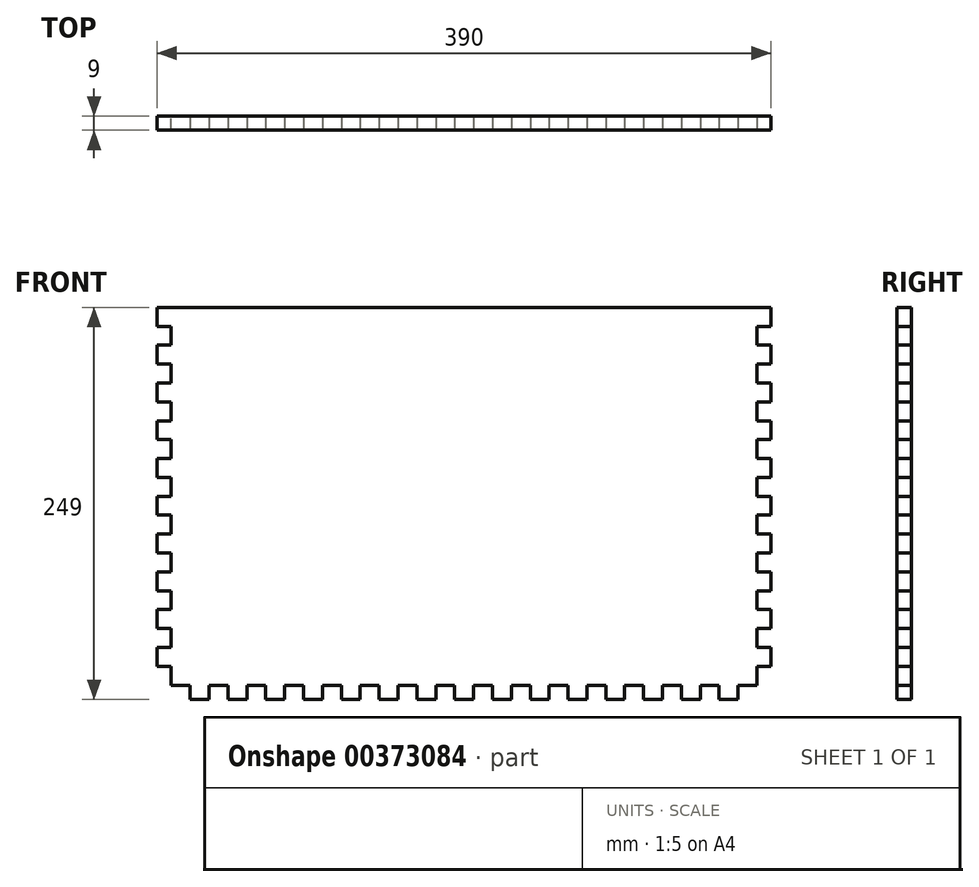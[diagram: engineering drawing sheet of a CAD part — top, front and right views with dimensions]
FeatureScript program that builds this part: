
annotation { "Feature Type Name" : "Feature", "Feature Type Description" : "" }
export const myFeature = defineFeature(function(context is Context, id is Id, definition is map)
    precondition{}
    {
        {
            var Q0;
            Q0=qCreatedBy(makeId("Front.planeOp"),FACE);
            var sketch = newSketch(context, id + "F0", { "sketchPlane" : qUnion([Q0])});
            skLineSegment(sketch, "E0.bottom", {"start": v(186, 120) * mm, "end": v(-186, 120) * mm});
            skLineSegment(sketch, "E0.top", {"start": v(186, -120) * mm, "end": v(-186, -120) * mm});
            skLineSegment(sketch, "E0.left", {"start": v(186, 120) * mm, "end": v(186, -120) * mm});
            skLineSegment(sketch, "E0.right", {"start": v(-186, 120) * mm, "end": v(-186, -120) * mm});
            skPoint(sketch, "E0.middle", {"position": v(0, 0) * mm});
            skSolve(sketch);
        }
        {
            var Q0;
            Q0=makeQuery(id+"F0.imprint","IMPRINT",FACE,{"disambiguationData":[TD([[makeQuery(id+"F0.imprint","IMPRINT",EDGE,{"derivedFrom":sQuery(id+"F0.wireOp",EDGE,"E0.bottom")}),1.0]])]});
            extrude(context, id + "F1", {"entities" : qUnion([Q0]), "depth" : 9 * mm});
        }
        {
            var Q0;
            Q0=makeQuery(id+"F1.opExtrude","CAP_FACE",FACE,{"disambiguationData":[OSD([sQuery(id+"F0.wireOp",EDGE,"E0.bottom"),sQuery(id+"F0.wireOp",EDGE,"E0.top"),sQuery(id+"F0.wireOp",EDGE,"E0.left"),sQuery(id+"F0.wireOp",EDGE,"E0.right")])],"isStart":false});
            var sketch = newSketch(context, id + "F2", { "sketchPlane" : qUnion([Q0])});
            skLineSegment(sketch, "E1.bottom", {"start": v(-186, 120) * mm, "end": v(-195, 120) * mm});
            skLineSegment(sketch, "E1.top", {"start": v(-186, 108) * mm, "end": v(-195, 108) * mm});
            skLineSegment(sketch, "E1.left", {"start": v(-186, 120) * mm, "end": v(-186, 108) * mm});
            skLineSegment(sketch, "E1.right", {"start": v(-195, 120) * mm, "end": v(-195, 108) * mm});
            skLineSegment(sketch, "E2.0.1.0", {"start": v(-186, 84) * mm, "end": v(-195, 84) * mm});
            skLineSegment(sketch, "E2.0.1.1", {"start": v(-195, 96) * mm, "end": v(-195, 84) * mm});
            skLineSegment(sketch, "E2.0.1.2", {"start": v(-186, 96) * mm, "end": v(-195, 96) * mm});
            skLineSegment(sketch, "E2.0.1.3", {"start": v(-186, 96) * mm, "end": v(-186, 84) * mm});
            skLineSegment(sketch, "E2.0.2.0", {"start": v(-186, 60) * mm, "end": v(-195, 60) * mm});
            skLineSegment(sketch, "E2.0.2.1", {"start": v(-195, 72) * mm, "end": v(-195, 60) * mm});
            skLineSegment(sketch, "E2.0.2.2", {"start": v(-186, 72) * mm, "end": v(-195, 72) * mm});
            skLineSegment(sketch, "E2.0.2.3", {"start": v(-186, 72) * mm, "end": v(-186, 60) * mm});
            skLineSegment(sketch, "E2.0.3.0", {"start": v(-186, 36) * mm, "end": v(-195, 36) * mm});
            skLineSegment(sketch, "E2.0.3.1", {"start": v(-195, 48) * mm, "end": v(-195, 36) * mm});
            skLineSegment(sketch, "E2.0.3.2", {"start": v(-186, 48) * mm, "end": v(-195, 48) * mm});
            skLineSegment(sketch, "E2.0.3.3", {"start": v(-186, 48) * mm, "end": v(-186, 36) * mm});
            skLineSegment(sketch, "E2.0.4.0", {"start": v(-186, 12) * mm, "end": v(-195, 12) * mm});
            skLineSegment(sketch, "E2.0.4.1", {"start": v(-195, 24) * mm, "end": v(-195, 12) * mm});
            skLineSegment(sketch, "E2.0.4.2", {"start": v(-186, 24) * mm, "end": v(-195, 24) * mm});
            skLineSegment(sketch, "E2.0.4.3", {"start": v(-186, 24) * mm, "end": v(-186, 12) * mm});
            skLineSegment(sketch, "E2.0.5.0", {"start": v(-186, -12) * mm, "end": v(-195, -12) * mm});
            skLineSegment(sketch, "E2.0.5.1", {"start": v(-195, 0) * mm, "end": v(-195, -12) * mm});
            skLineSegment(sketch, "E2.0.5.2", {"start": v(-186, 0) * mm, "end": v(-195, 0) * mm});
            skLineSegment(sketch, "E2.0.5.3", {"start": v(-186, 0) * mm, "end": v(-186, -12) * mm});
            skLineSegment(sketch, "E2.0.6.0", {"start": v(-186, -36) * mm, "end": v(-195, -36) * mm});
            skLineSegment(sketch, "E2.0.6.1", {"start": v(-195, -24) * mm, "end": v(-195, -36) * mm});
            skLineSegment(sketch, "E2.0.6.2", {"start": v(-186, -24) * mm, "end": v(-195, -24) * mm});
            skLineSegment(sketch, "E2.0.6.3", {"start": v(-186, -24) * mm, "end": v(-186, -36) * mm});
            skLineSegment(sketch, "E2.0.7.0", {"start": v(-186, -60) * mm, "end": v(-195, -60) * mm});
            skLineSegment(sketch, "E2.0.7.1", {"start": v(-195, -48) * mm, "end": v(-195, -60) * mm});
            skLineSegment(sketch, "E2.0.7.2", {"start": v(-186, -48) * mm, "end": v(-195, -48) * mm});
            skLineSegment(sketch, "E2.0.7.3", {"start": v(-186, -48) * mm, "end": v(-186, -60) * mm});
            skLineSegment(sketch, "E2.0.8.0", {"start": v(-186, -84) * mm, "end": v(-195, -84) * mm});
            skLineSegment(sketch, "E2.0.8.1", {"start": v(-195, -72) * mm, "end": v(-195, -84) * mm});
            skLineSegment(sketch, "E2.0.8.2", {"start": v(-186, -72) * mm, "end": v(-195, -72) * mm});
            skLineSegment(sketch, "E2.0.8.3", {"start": v(-186, -72) * mm, "end": v(-186, -84) * mm});
            skLineSegment(sketch, "E2.0.9.0", {"start": v(-186, -108) * mm, "end": v(-195, -108) * mm});
            skLineSegment(sketch, "E2.0.9.1", {"start": v(-195, -96) * mm, "end": v(-195, -108) * mm});
            skLineSegment(sketch, "E2.0.9.2", {"start": v(-186, -96) * mm, "end": v(-195, -96) * mm});
            skLineSegment(sketch, "E2.0.9.3", {"start": v(-186, -96) * mm, "end": v(-186, -108) * mm});
            skLineSegment(sketch, "E2.direction1", {"start": v(-195, 108) * mm, "end": v(-186, 108) * mm, "construction": true});
            skLineSegment(sketch, "E2.direction2", {"start": v(-195, 108) * mm, "end": v(-195, 84) * mm, "construction": true});
            skLineSegment(sketch, "E3", {"start": v(0, 120) * mm, "end": v(0, 0) * mm});
            skLineSegment(sketch, "E4.MirrorCS", {"start": v(186, 108) * mm, "end": v(195, 108) * mm});
            skLineSegment(sketch, "E5.MirrorCS", {"start": v(195, 108) * mm, "end": v(186, 108) * mm, "construction": true});
            skLineSegment(sketch, "E6.MirrorCS", {"start": v(195, 96) * mm, "end": v(195, 84) * mm});
            skLineSegment(sketch, "E7.MirrorCS", {"start": v(186, -24) * mm, "end": v(186, -36) * mm});
            skLineSegment(sketch, "E8.MirrorCS", {"start": v(186, -96) * mm, "end": v(186, -108) * mm});
            skLineSegment(sketch, "E9.MirrorCS", {"start": v(186, 0) * mm, "end": v(186, -12) * mm});
            skLineSegment(sketch, "E10.MirrorCS", {"start": v(186, -108) * mm, "end": v(195, -108) * mm});
            skLineSegment(sketch, "E11.MirrorCS", {"start": v(195, -48) * mm, "end": v(195, -60) * mm});
            skLineSegment(sketch, "E12.MirrorCS", {"start": v(186, -12) * mm, "end": v(195, -12) * mm});
            skLineSegment(sketch, "E13.MirrorCS", {"start": v(186, -84) * mm, "end": v(195, -84) * mm});
            skLineSegment(sketch, "E14.MirrorCS", {"start": v(186, 12) * mm, "end": v(195, 12) * mm});
            skLineSegment(sketch, "E15.MirrorCS", {"start": v(186, -60) * mm, "end": v(195, -60) * mm});
            skLineSegment(sketch, "E16.MirrorCS", {"start": v(186, -36) * mm, "end": v(195, -36) * mm});
            skLineSegment(sketch, "E17.MirrorCS", {"start": v(195, -96) * mm, "end": v(195, -108) * mm});
            skLineSegment(sketch, "E18.MirrorCS", {"start": v(186, -48) * mm, "end": v(195, -48) * mm});
            skLineSegment(sketch, "E19.MirrorCS", {"start": v(195, 0) * mm, "end": v(195, -12) * mm});
            skLineSegment(sketch, "E20.MirrorCS", {"start": v(195, -72) * mm, "end": v(195, -84) * mm});
            skLineSegment(sketch, "E21.MirrorCS", {"start": v(195, 24) * mm, "end": v(195, 12) * mm});
            skLineSegment(sketch, "E22.MirrorCS", {"start": v(195, 48) * mm, "end": v(195, 36) * mm});
            skLineSegment(sketch, "E23.MirrorCS", {"start": v(186, 48) * mm, "end": v(195, 48) * mm});
            skLineSegment(sketch, "E24.MirrorCS", {"start": v(186, 48) * mm, "end": v(186, 36) * mm});
            skLineSegment(sketch, "E25.MirrorCS", {"start": v(186, 120) * mm, "end": v(195, 120) * mm});
            skLineSegment(sketch, "E26.MirrorCS", {"start": v(186, 120) * mm, "end": v(186, 108) * mm});
            skLineSegment(sketch, "E27.MirrorCS", {"start": v(195, 120) * mm, "end": v(195, 108) * mm});
            skLineSegment(sketch, "E28.MirrorCS", {"start": v(186, 84) * mm, "end": v(195, 84) * mm});
            skLineSegment(sketch, "E29.MirrorCS", {"start": v(186, 96) * mm, "end": v(195, 96) * mm});
            skLineSegment(sketch, "E30.MirrorCS", {"start": v(186, 96) * mm, "end": v(186, 84) * mm});
            skLineSegment(sketch, "E31.MirrorCS", {"start": v(186, 60) * mm, "end": v(195, 60) * mm});
            skLineSegment(sketch, "E32.MirrorCS", {"start": v(195, 72) * mm, "end": v(195, 60) * mm});
            skLineSegment(sketch, "E33.MirrorCS", {"start": v(186, 72) * mm, "end": v(195, 72) * mm});
            skLineSegment(sketch, "E34.MirrorCS", {"start": v(186, 72) * mm, "end": v(186, 60) * mm});
            skLineSegment(sketch, "E35.MirrorCS", {"start": v(195, 108) * mm, "end": v(195, 84) * mm, "construction": true});
            skLineSegment(sketch, "E36.MirrorCS", {"start": v(195, -24) * mm, "end": v(195, -36) * mm});
            skLineSegment(sketch, "E37.MirrorCS", {"start": v(186, 36) * mm, "end": v(195, 36) * mm});
            skLineSegment(sketch, "E38.MirrorCS", {"start": v(186, -96) * mm, "end": v(195, -96) * mm});
            skLineSegment(sketch, "E39.MirrorCS", {"start": v(186, -48) * mm, "end": v(186, -60) * mm});
            skLineSegment(sketch, "E40.MirrorCS", {"start": v(186, 0) * mm, "end": v(195, 0) * mm});
            skLineSegment(sketch, "E41.MirrorCS", {"start": v(186, -72) * mm, "end": v(195, -72) * mm});
            skLineSegment(sketch, "E42.MirrorCS", {"start": v(186, 24) * mm, "end": v(195, 24) * mm});
            skLineSegment(sketch, "E43.MirrorCS", {"start": v(186, -24) * mm, "end": v(195, -24) * mm});
            skLineSegment(sketch, "E44.MirrorCS", {"start": v(186, -72) * mm, "end": v(186, -84) * mm});
            skLineSegment(sketch, "E45.MirrorCS", {"start": v(186, 24) * mm, "end": v(186, 12) * mm});
            skSolve(sketch);
        }
        {
            var Q0;
            Q0 = qSketchRegion(id + "F2", true);
            var Q1;
            Q1=makeQuery(id+"F1.opExtrude","CAP_FACE",FACE,{"disambiguationData":[OSD([sQuery(id+"F0.wireOp",EDGE,"E0.bottom"),sQuery(id+"F0.wireOp",EDGE,"E0.top"),sQuery(id+"F0.wireOp",EDGE,"E0.left"),sQuery(id+"F0.wireOp",EDGE,"E0.right")])],"isStart":true});
            extrude(context, id + "F3", {"entities" : qUnion([Q0]), "operationType" : NewBodyOperationType.ADD, "endBound" : BoundingType.UP_TO_SURFACE, "oppositeDirection" : true, "endBoundEntityFace" : qUnion([Q1]), "depth" : 25 * mm});
        }
        {
            var Q0;
            Q0=makeQuery(id+"F3.boolean.opBoolean","MERGE",FACE,{"derivedFrom":[makeQuery(id+"F1.opExtrude","CAP_FACE",FACE,{"disambiguationData":[OSD([sQuery(id+"F0.wireOp",EDGE,"E0.bottom"),sQuery(id+"F0.wireOp",EDGE,"E0.top"),sQuery(id+"F0.wireOp",EDGE,"E0.left"),sQuery(id+"F0.wireOp",EDGE,"E0.right")])],"isStart":false}),makeQuery(id+"F3.opExtrude","CAP_FACE",FACE,{"disambiguationData":[OSD([sQuery(id+"F2.wireOp",EDGE,"E1.bottom"),sQuery(id+"F2.wireOp",EDGE,"E1.top"),sQuery(id+"F2.wireOp",EDGE,"E1.left"),sQuery(id+"F2.wireOp",EDGE,"E1.right")])],"isStart":true}),makeQuery(id+"F3.opExtrude","CAP_FACE",FACE,{"disambiguationData":[OSD([sQuery(id+"F2.wireOp",EDGE,"E2.0.1.0"),sQuery(id+"F2.wireOp",EDGE,"E2.0.1.1"),sQuery(id+"F2.wireOp",EDGE,"E2.0.1.2"),sQuery(id+"F2.wireOp",EDGE,"E2.0.1.3")])],"isStart":true}),makeQuery(id+"F3.opExtrude","CAP_FACE",FACE,{"disambiguationData":[OSD([sQuery(id+"F2.wireOp",EDGE,"E2.0.2.0"),sQuery(id+"F2.wireOp",EDGE,"E2.0.2.1"),sQuery(id+"F2.wireOp",EDGE,"E2.0.2.2"),sQuery(id+"F2.wireOp",EDGE,"E2.0.2.3")])],"isStart":true}),makeQuery(id+"F3.opExtrude","CAP_FACE",FACE,{"disambiguationData":[OSD([sQuery(id+"F2.wireOp",EDGE,"E2.0.3.0"),sQuery(id+"F2.wireOp",EDGE,"E2.0.3.1"),sQuery(id+"F2.wireOp",EDGE,"E2.0.3.2"),sQuery(id+"F2.wireOp",EDGE,"E2.0.3.3")])],"isStart":true}),makeQuery(id+"F3.opExtrude","CAP_FACE",FACE,{"disambiguationData":[OSD([sQuery(id+"F2.wireOp",EDGE,"E2.0.4.0"),sQuery(id+"F2.wireOp",EDGE,"E2.0.4.1"),sQuery(id+"F2.wireOp",EDGE,"E2.0.4.2"),sQuery(id+"F2.wireOp",EDGE,"E2.0.4.3")])],"isStart":true}),makeQuery(id+"F3.opExtrude","CAP_FACE",FACE,{"disambiguationData":[OSD([sQuery(id+"F2.wireOp",EDGE,"E2.0.5.0"),sQuery(id+"F2.wireOp",EDGE,"E2.0.5.1"),sQuery(id+"F2.wireOp",EDGE,"E2.0.5.2"),sQuery(id+"F2.wireOp",EDGE,"E2.0.5.3")])],"isStart":true}),makeQuery(id+"F3.opExtrude","CAP_FACE",FACE,{"disambiguationData":[OSD([sQuery(id+"F2.wireOp",EDGE,"E2.0.6.0"),sQuery(id+"F2.wireOp",EDGE,"E2.0.6.1"),sQuery(id+"F2.wireOp",EDGE,"E2.0.6.2"),sQuery(id+"F2.wireOp",EDGE,"E2.0.6.3")])],"isStart":true}),makeQuery(id+"F3.opExtrude","CAP_FACE",FACE,{"disambiguationData":[OSD([sQuery(id+"F2.wireOp",EDGE,"E2.0.7.0"),sQuery(id+"F2.wireOp",EDGE,"E2.0.7.1"),sQuery(id+"F2.wireOp",EDGE,"E2.0.7.2"),sQuery(id+"F2.wireOp",EDGE,"E2.0.7.3")])],"isStart":true}),makeQuery(id+"F3.opExtrude","CAP_FACE",FACE,{"disambiguationData":[OSD([sQuery(id+"F2.wireOp",EDGE,"E2.0.8.0"),sQuery(id+"F2.wireOp",EDGE,"E2.0.8.1"),sQuery(id+"F2.wireOp",EDGE,"E2.0.8.2"),sQuery(id+"F2.wireOp",EDGE,"E2.0.8.3")])],"isStart":true}),makeQuery(id+"F3.opExtrude","CAP_FACE",FACE,{"disambiguationData":[OSD([sQuery(id+"F2.wireOp",EDGE,"E2.0.9.0"),sQuery(id+"F2.wireOp",EDGE,"E2.0.9.1"),sQuery(id+"F2.wireOp",EDGE,"E2.0.9.2"),sQuery(id+"F2.wireOp",EDGE,"E2.0.9.3")])],"isStart":true}),makeQuery(id+"F3.opExtrude","CAP_FACE",FACE,{"disambiguationData":[OSD([sQuery(id+"F2.wireOp",EDGE,"E4.MirrorCS"),sQuery(id+"F2.wireOp",EDGE,"E25.MirrorCS"),sQuery(id+"F2.wireOp",EDGE,"E26.MirrorCS"),sQuery(id+"F2.wireOp",EDGE,"E27.MirrorCS")])],"isStart":true}),makeQuery(id+"F3.opExtrude","CAP_FACE",FACE,{"disambiguationData":[OSD([sQuery(id+"F2.wireOp",EDGE,"E6.MirrorCS"),sQuery(id+"F2.wireOp",EDGE,"E28.MirrorCS"),sQuery(id+"F2.wireOp",EDGE,"E29.MirrorCS"),sQuery(id+"F2.wireOp",EDGE,"E30.MirrorCS")])],"isStart":true}),makeQuery(id+"F3.opExtrude","CAP_FACE",FACE,{"disambiguationData":[OSD([sQuery(id+"F2.wireOp",EDGE,"E7.MirrorCS"),sQuery(id+"F2.wireOp",EDGE,"E16.MirrorCS"),sQuery(id+"F2.wireOp",EDGE,"E36.MirrorCS"),sQuery(id+"F2.wireOp",EDGE,"E43.MirrorCS")])],"isStart":true}),makeQuery(id+"F3.opExtrude","CAP_FACE",FACE,{"disambiguationData":[OSD([sQuery(id+"F2.wireOp",EDGE,"E8.MirrorCS"),sQuery(id+"F2.wireOp",EDGE,"E10.MirrorCS"),sQuery(id+"F2.wireOp",EDGE,"E17.MirrorCS"),sQuery(id+"F2.wireOp",EDGE,"E38.MirrorCS")])],"isStart":true}),makeQuery(id+"F3.opExtrude","CAP_FACE",FACE,{"disambiguationData":[OSD([sQuery(id+"F2.wireOp",EDGE,"E9.MirrorCS"),sQuery(id+"F2.wireOp",EDGE,"E12.MirrorCS"),sQuery(id+"F2.wireOp",EDGE,"E19.MirrorCS"),sQuery(id+"F2.wireOp",EDGE,"E40.MirrorCS")])],"isStart":true}),makeQuery(id+"F3.opExtrude","CAP_FACE",FACE,{"disambiguationData":[OSD([sQuery(id+"F2.wireOp",EDGE,"E11.MirrorCS"),sQuery(id+"F2.wireOp",EDGE,"E15.MirrorCS"),sQuery(id+"F2.wireOp",EDGE,"E18.MirrorCS"),sQuery(id+"F2.wireOp",EDGE,"E39.MirrorCS")])],"isStart":true}),makeQuery(id+"F3.opExtrude","CAP_FACE",FACE,{"disambiguationData":[OSD([sQuery(id+"F2.wireOp",EDGE,"E13.MirrorCS"),sQuery(id+"F2.wireOp",EDGE,"E20.MirrorCS"),sQuery(id+"F2.wireOp",EDGE,"E41.MirrorCS"),sQuery(id+"F2.wireOp",EDGE,"E44.MirrorCS")])],"isStart":true}),makeQuery(id+"F3.opExtrude","CAP_FACE",FACE,{"disambiguationData":[OSD([sQuery(id+"F2.wireOp",EDGE,"E14.MirrorCS"),sQuery(id+"F2.wireOp",EDGE,"E21.MirrorCS"),sQuery(id+"F2.wireOp",EDGE,"E42.MirrorCS"),sQuery(id+"F2.wireOp",EDGE,"E45.MirrorCS")])],"isStart":true}),makeQuery(id+"F3.opExtrude","CAP_FACE",FACE,{"disambiguationData":[OSD([sQuery(id+"F2.wireOp",EDGE,"E22.MirrorCS"),sQuery(id+"F2.wireOp",EDGE,"E23.MirrorCS"),sQuery(id+"F2.wireOp",EDGE,"E24.MirrorCS"),sQuery(id+"F2.wireOp",EDGE,"E37.MirrorCS")])],"isStart":true}),makeQuery(id+"F3.opExtrude","CAP_FACE",FACE,{"disambiguationData":[OSD([sQuery(id+"F2.wireOp",EDGE,"E31.MirrorCS"),sQuery(id+"F2.wireOp",EDGE,"E32.MirrorCS"),sQuery(id+"F2.wireOp",EDGE,"E33.MirrorCS"),sQuery(id+"F2.wireOp",EDGE,"E34.MirrorCS")])],"isStart":true})]});
            var sketch = newSketch(context, id + "F4", { "sketchPlane" : qUnion([Q0])});
            skLineSegment(sketch, "E46", {"start": v(0, -120) * mm, "end": v(0, -129) * mm, "construction": true});
            skPoint(sketch, "E46.endSnap0", {"position": v(0, -120) * mm});
            skLineSegment(sketch, "E47.bottom", {"start": v(6, -129) * mm, "end": v(-6, -129) * mm});
            skLineSegment(sketch, "E47.top", {"start": v(6, -120) * mm, "end": v(-6, -120) * mm});
            skLineSegment(sketch, "E47.left", {"start": v(6, -129) * mm, "end": v(6, -120) * mm});
            skLineSegment(sketch, "E47.right", {"start": v(-6, -129) * mm, "end": v(-6, -120) * mm});
            skPoint(sketch, "E47.middle", {"position": v(0, -124.5) * mm});
            skLineSegment(sketch, "E48.1.0.0", {"start": v(30, -129) * mm, "end": v(30, -120) * mm});
            skLineSegment(sketch, "E48.1.0.1", {"start": v(30, -120) * mm, "end": v(18, -120) * mm});
            skLineSegment(sketch, "E48.1.0.2", {"start": v(18, -129) * mm, "end": v(18, -120) * mm});
            skLineSegment(sketch, "E48.1.0.3", {"start": v(30, -129) * mm, "end": v(18, -129) * mm});
            skLineSegment(sketch, "E48.2.0.0", {"start": v(54, -129) * mm, "end": v(54, -120) * mm});
            skLineSegment(sketch, "E48.2.0.1", {"start": v(54, -120) * mm, "end": v(42, -120) * mm});
            skLineSegment(sketch, "E48.2.0.2", {"start": v(42, -129) * mm, "end": v(42, -120) * mm});
            skLineSegment(sketch, "E48.2.0.3", {"start": v(54, -129) * mm, "end": v(42, -129) * mm});
            skLineSegment(sketch, "E48.3.0.0", {"start": v(78, -129) * mm, "end": v(78, -120) * mm});
            skLineSegment(sketch, "E48.3.0.1", {"start": v(78, -120) * mm, "end": v(66, -120) * mm});
            skLineSegment(sketch, "E48.3.0.2", {"start": v(66, -129) * mm, "end": v(66, -120) * mm});
            skLineSegment(sketch, "E48.3.0.3", {"start": v(78, -129) * mm, "end": v(66, -129) * mm});
            skLineSegment(sketch, "E48.4.0.0", {"start": v(102, -129) * mm, "end": v(102, -120) * mm});
            skLineSegment(sketch, "E48.4.0.1", {"start": v(102, -120) * mm, "end": v(90, -120) * mm});
            skLineSegment(sketch, "E48.4.0.2", {"start": v(90, -129) * mm, "end": v(90, -120) * mm});
            skLineSegment(sketch, "E48.4.0.3", {"start": v(102, -129) * mm, "end": v(90, -129) * mm});
            skLineSegment(sketch, "E48.5.0.0", {"start": v(126, -129) * mm, "end": v(126, -120) * mm});
            skLineSegment(sketch, "E48.5.0.1", {"start": v(126, -120) * mm, "end": v(114, -120) * mm});
            skLineSegment(sketch, "E48.5.0.2", {"start": v(114, -129) * mm, "end": v(114, -120) * mm});
            skLineSegment(sketch, "E48.5.0.3", {"start": v(126, -129) * mm, "end": v(114, -129) * mm});
            skLineSegment(sketch, "E48.6.0.0", {"start": v(150, -129) * mm, "end": v(150, -120) * mm});
            skLineSegment(sketch, "E48.6.0.1", {"start": v(150, -120) * mm, "end": v(138, -120) * mm});
            skLineSegment(sketch, "E48.6.0.2", {"start": v(138, -129) * mm, "end": v(138, -120) * mm});
            skLineSegment(sketch, "E48.6.0.3", {"start": v(150, -129) * mm, "end": v(138, -129) * mm});
            skLineSegment(sketch, "E48.7.0.0", {"start": v(174, -129) * mm, "end": v(174, -120) * mm});
            skLineSegment(sketch, "E48.7.0.1", {"start": v(174, -120) * mm, "end": v(162, -120) * mm});
            skLineSegment(sketch, "E48.7.0.2", {"start": v(162, -129) * mm, "end": v(162, -120) * mm});
            skLineSegment(sketch, "E48.7.0.3", {"start": v(174, -129) * mm, "end": v(162, -129) * mm});
            skLineSegment(sketch, "E48.direction1", {"start": v(6, -129) * mm, "end": v(30, -129) * mm, "construction": true});
            skLineSegment(sketch, "E49.MirrorCS", {"start": v(-30, -129) * mm, "end": v(-30, -120) * mm});
            skLineSegment(sketch, "E50.MirrorCS", {"start": v(-102, -129) * mm, "end": v(-102, -120) * mm});
            skLineSegment(sketch, "E51.MirrorCS", {"start": v(-126, -129) * mm, "end": v(-126, -120) * mm});
            skLineSegment(sketch, "E52.MirrorCS", {"start": v(-174, -120) * mm, "end": v(-162, -120) * mm});
            skLineSegment(sketch, "E53.MirrorCS", {"start": v(-126, -129) * mm, "end": v(-114, -129) * mm});
            skLineSegment(sketch, "E54.MirrorCS", {"start": v(-54, -129) * mm, "end": v(-42, -129) * mm});
            skLineSegment(sketch, "E55.MirrorCS", {"start": v(-42, -129) * mm, "end": v(-42, -120) * mm});
            skLineSegment(sketch, "E56.MirrorCS", {"start": v(-150, -129) * mm, "end": v(-138, -129) * mm});
            skLineSegment(sketch, "E57.MirrorCS", {"start": v(-54, -120) * mm, "end": v(-42, -120) * mm});
            skLineSegment(sketch, "E58.MirrorCS", {"start": v(-54, -129) * mm, "end": v(-54, -120) * mm});
            skLineSegment(sketch, "E59.MirrorCS", {"start": v(-30, -129) * mm, "end": v(-18, -129) * mm});
            skLineSegment(sketch, "E60.MirrorCS", {"start": v(-18, -129) * mm, "end": v(-18, -120) * mm});
            skLineSegment(sketch, "E61.MirrorCS", {"start": v(-30, -120) * mm, "end": v(-18, -120) * mm});
            skLineSegment(sketch, "E62.MirrorCS", {"start": v(-114, -129) * mm, "end": v(-114, -120) * mm});
            skLineSegment(sketch, "E63.MirrorCS", {"start": v(-66, -129) * mm, "end": v(-66, -120) * mm});
            skLineSegment(sketch, "E64.MirrorCS", {"start": v(-78, -120) * mm, "end": v(-66, -120) * mm});
            skLineSegment(sketch, "E65.MirrorCS", {"start": v(-78, -129) * mm, "end": v(-78, -120) * mm});
            skLineSegment(sketch, "E66.MirrorCS", {"start": v(-102, -129) * mm, "end": v(-90, -129) * mm});
            skLineSegment(sketch, "E67.MirrorCS", {"start": v(-174, -129) * mm, "end": v(-174, -120) * mm});
            skLineSegment(sketch, "E68.MirrorCS", {"start": v(-138, -129) * mm, "end": v(-138, -120) * mm});
            skLineSegment(sketch, "E69.MirrorCS", {"start": v(-78, -129) * mm, "end": v(-66, -129) * mm});
            skLineSegment(sketch, "E70.MirrorCS", {"start": v(-174, -129) * mm, "end": v(-162, -129) * mm});
            skLineSegment(sketch, "E71.MirrorCS", {"start": v(-150, -129) * mm, "end": v(-150, -120) * mm});
            skLineSegment(sketch, "E72.MirrorCS", {"start": v(-162, -129) * mm, "end": v(-162, -120) * mm});
            skLineSegment(sketch, "E73.MirrorCS", {"start": v(-126, -120) * mm, "end": v(-114, -120) * mm});
            skLineSegment(sketch, "E74.MirrorCS", {"start": v(-102, -120) * mm, "end": v(-90, -120) * mm});
            skLineSegment(sketch, "E75.MirrorCS", {"start": v(-150, -120) * mm, "end": v(-138, -120) * mm});
            skLineSegment(sketch, "E76.MirrorCS", {"start": v(-90, -129) * mm, "end": v(-90, -120) * mm});
            skSolve(sketch);
        }
        {
            var Q0;
            Q0 = qSketchRegion(id + "F4", true);
            var Q1;
            {var subQ0=sQuery(id+"F0.wireOp",EDGE,"E0.right");var subQ1=sQuery(id+"F0.wireOp",EDGE,"E0.left");var subQ2=sQuery(id+"F0.wireOp",EDGE,"E0.top");var subQ3=sQuery(id+"F0.wireOp",EDGE,"E0.bottom");Q1=makeQuery(id+"F3.boolean.opBoolean","MERGE",FACE,{"derivedFrom":[makeQuery(id+"F1.opExtrude","CAP_FACE",FACE,{"disambiguationData":[OSD([subQ3,subQ2,subQ1,subQ0])],"isStart":true}),makeQuery(id+"F3.opExtrude","CAP_FACE",FACE,{"disambiguationData":[OSD([subQ3,subQ2,subQ1,subQ0]),ownerDisambiguation([makeQuery(id+"F2.imprint","IMPRINT",EDGE,{"derivedFrom":sQuery(id+"F2.wireOp",EDGE,"E1.bottom")})])],"isStart":false}),makeQuery(id+"F3.opExtrude","CAP_FACE",FACE,{"disambiguationData":[OSD([subQ3,subQ2,subQ1,subQ0]),ownerDisambiguation([makeQuery(id+"F2.imprint","IMPRINT",EDGE,{"derivedFrom":sQuery(id+"F2.wireOp",EDGE,"E2.0.1.0")})])],"isStart":false}),makeQuery(id+"F3.opExtrude","CAP_FACE",FACE,{"disambiguationData":[OSD([subQ3,subQ2,subQ1,subQ0]),ownerDisambiguation([makeQuery(id+"F2.imprint","IMPRINT",EDGE,{"derivedFrom":sQuery(id+"F2.wireOp",EDGE,"E2.0.2.0")})])],"isStart":false}),makeQuery(id+"F3.opExtrude","CAP_FACE",FACE,{"disambiguationData":[OSD([subQ3,subQ2,subQ1,subQ0]),ownerDisambiguation([makeQuery(id+"F2.imprint","IMPRINT",EDGE,{"derivedFrom":sQuery(id+"F2.wireOp",EDGE,"E2.0.3.0")})])],"isStart":false}),makeQuery(id+"F3.opExtrude","CAP_FACE",FACE,{"disambiguationData":[OSD([subQ3,subQ2,subQ1,subQ0]),ownerDisambiguation([makeQuery(id+"F2.imprint","IMPRINT",EDGE,{"derivedFrom":sQuery(id+"F2.wireOp",EDGE,"E2.0.4.0")})])],"isStart":false}),makeQuery(id+"F3.opExtrude","CAP_FACE",FACE,{"disambiguationData":[OSD([subQ3,subQ2,subQ1,subQ0]),ownerDisambiguation([makeQuery(id+"F2.imprint","IMPRINT",EDGE,{"derivedFrom":sQuery(id+"F2.wireOp",EDGE,"E2.0.5.0")})])],"isStart":false}),makeQuery(id+"F3.opExtrude","CAP_FACE",FACE,{"disambiguationData":[OSD([subQ3,subQ2,subQ1,subQ0]),ownerDisambiguation([makeQuery(id+"F2.imprint","IMPRINT",EDGE,{"derivedFrom":sQuery(id+"F2.wireOp",EDGE,"E2.0.6.0")})])],"isStart":false}),makeQuery(id+"F3.opExtrude","CAP_FACE",FACE,{"disambiguationData":[OSD([subQ3,subQ2,subQ1,subQ0]),ownerDisambiguation([makeQuery(id+"F2.imprint","IMPRINT",EDGE,{"derivedFrom":sQuery(id+"F2.wireOp",EDGE,"E2.0.7.0")})])],"isStart":false}),makeQuery(id+"F3.opExtrude","CAP_FACE",FACE,{"disambiguationData":[OSD([subQ3,subQ2,subQ1,subQ0]),ownerDisambiguation([makeQuery(id+"F2.imprint","IMPRINT",EDGE,{"derivedFrom":sQuery(id+"F2.wireOp",EDGE,"E2.0.8.0")})])],"isStart":false}),makeQuery(id+"F3.opExtrude","CAP_FACE",FACE,{"disambiguationData":[OSD([subQ3,subQ2,subQ1,subQ0]),ownerDisambiguation([makeQuery(id+"F2.imprint","IMPRINT",EDGE,{"derivedFrom":sQuery(id+"F2.wireOp",EDGE,"E2.0.9.0")})])],"isStart":false}),makeQuery(id+"F3.opExtrude","CAP_FACE",FACE,{"disambiguationData":[OSD([subQ3,subQ2,subQ1,subQ0]),ownerDisambiguation([makeQuery(id+"F2.imprint","IMPRINT",EDGE,{"derivedFrom":sQuery(id+"F2.wireOp",EDGE,"E4.MirrorCS")})])],"isStart":false}),makeQuery(id+"F3.opExtrude","CAP_FACE",FACE,{"disambiguationData":[OSD([subQ3,subQ2,subQ1,subQ0]),ownerDisambiguation([makeQuery(id+"F2.imprint","IMPRINT",EDGE,{"derivedFrom":sQuery(id+"F2.wireOp",EDGE,"E6.MirrorCS")})])],"isStart":false}),makeQuery(id+"F3.opExtrude","CAP_FACE",FACE,{"disambiguationData":[OSD([subQ3,subQ2,subQ1,subQ0]),ownerDisambiguation([makeQuery(id+"F2.imprint","IMPRINT",EDGE,{"derivedFrom":sQuery(id+"F2.wireOp",EDGE,"E7.MirrorCS")})])],"isStart":false}),makeQuery(id+"F3.opExtrude","CAP_FACE",FACE,{"disambiguationData":[OSD([subQ3,subQ2,subQ1,subQ0]),ownerDisambiguation([makeQuery(id+"F2.imprint","IMPRINT",EDGE,{"derivedFrom":sQuery(id+"F2.wireOp",EDGE,"E8.MirrorCS")})])],"isStart":false}),makeQuery(id+"F3.opExtrude","CAP_FACE",FACE,{"disambiguationData":[OSD([subQ3,subQ2,subQ1,subQ0]),ownerDisambiguation([makeQuery(id+"F2.imprint","IMPRINT",EDGE,{"derivedFrom":sQuery(id+"F2.wireOp",EDGE,"E9.MirrorCS")})])],"isStart":false}),makeQuery(id+"F3.opExtrude","CAP_FACE",FACE,{"disambiguationData":[OSD([subQ3,subQ2,subQ1,subQ0]),ownerDisambiguation([makeQuery(id+"F2.imprint","IMPRINT",EDGE,{"derivedFrom":sQuery(id+"F2.wireOp",EDGE,"E11.MirrorCS")})])],"isStart":false}),makeQuery(id+"F3.opExtrude","CAP_FACE",FACE,{"disambiguationData":[OSD([subQ3,subQ2,subQ1,subQ0]),ownerDisambiguation([makeQuery(id+"F2.imprint","IMPRINT",EDGE,{"derivedFrom":sQuery(id+"F2.wireOp",EDGE,"E13.MirrorCS")})])],"isStart":false}),makeQuery(id+"F3.opExtrude","CAP_FACE",FACE,{"disambiguationData":[OSD([subQ3,subQ2,subQ1,subQ0]),ownerDisambiguation([makeQuery(id+"F2.imprint","IMPRINT",EDGE,{"derivedFrom":sQuery(id+"F2.wireOp",EDGE,"E14.MirrorCS")})])],"isStart":false}),makeQuery(id+"F3.opExtrude","CAP_FACE",FACE,{"disambiguationData":[OSD([subQ3,subQ2,subQ1,subQ0]),ownerDisambiguation([makeQuery(id+"F2.imprint","IMPRINT",EDGE,{"derivedFrom":sQuery(id+"F2.wireOp",EDGE,"E22.MirrorCS")})])],"isStart":false}),makeQuery(id+"F3.opExtrude","CAP_FACE",FACE,{"disambiguationData":[OSD([subQ3,subQ2,subQ1,subQ0]),ownerDisambiguation([makeQuery(id+"F2.imprint","IMPRINT",EDGE,{"derivedFrom":sQuery(id+"F2.wireOp",EDGE,"E31.MirrorCS")})])],"isStart":false})]});}
            extrude(context, id + "F5", {"entities" : qUnion([Q0]), "operationType" : NewBodyOperationType.ADD, "endBound" : BoundingType.UP_TO_SURFACE, "oppositeDirection" : true, "endBoundEntityFace" : qUnion([Q1]), "depth" : 25 * mm});
        }
    });
